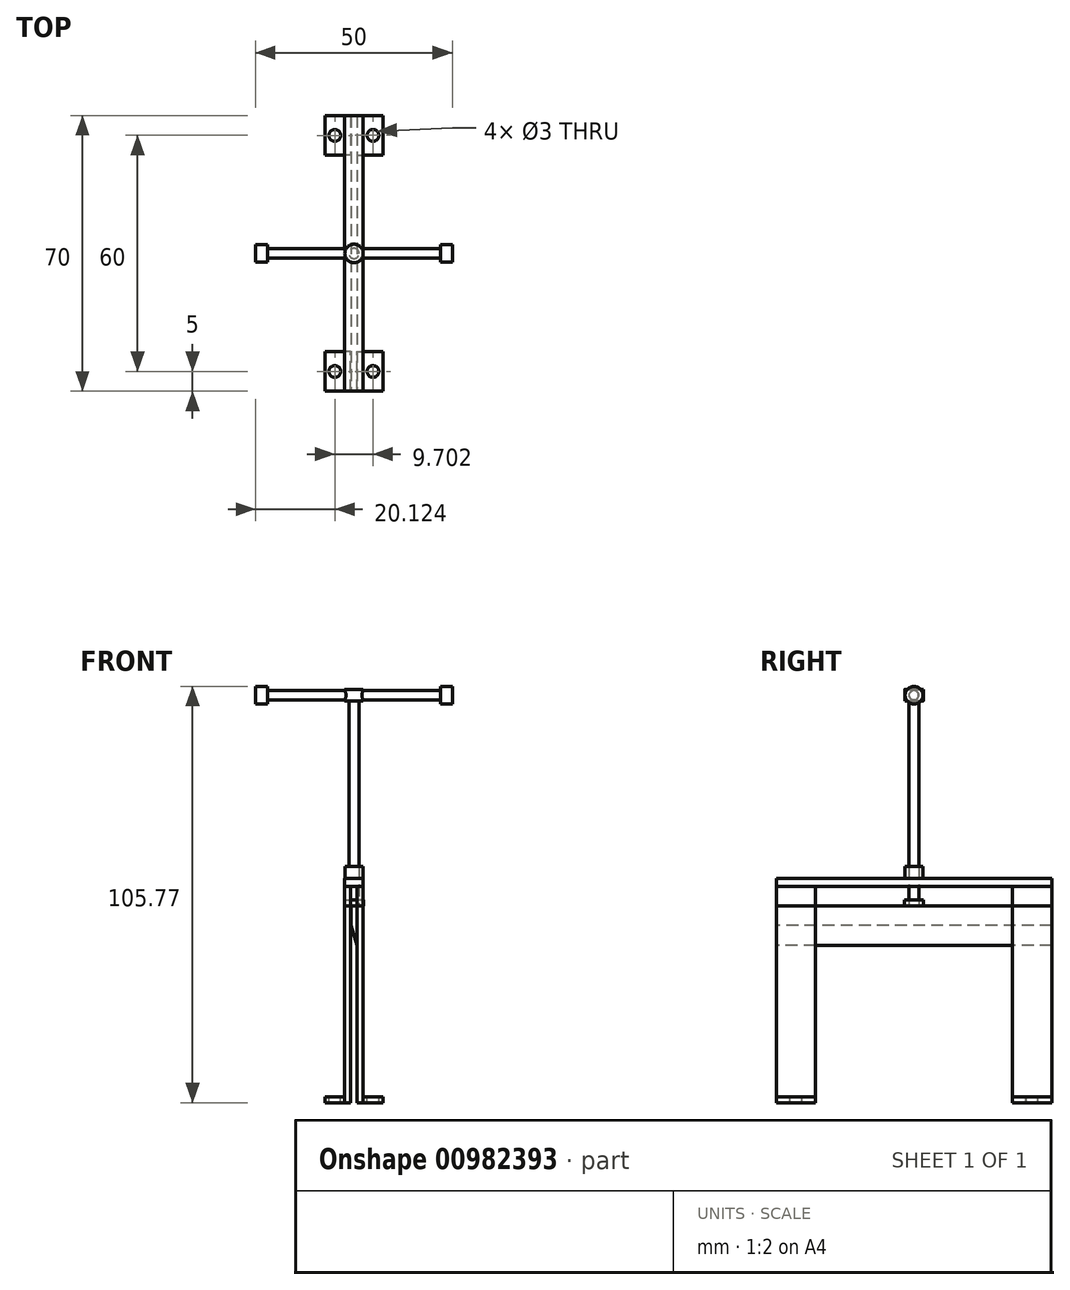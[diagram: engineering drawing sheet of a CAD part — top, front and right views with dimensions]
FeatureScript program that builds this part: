
annotation { "Feature Type Name" : "Feature", "Feature Type Description" : "" }
export const myFeature = defineFeature(function(context is Context, id is Id, definition is map)
    precondition{}
    {
        {
            var Q0;
            Q0=qCreatedBy(makeId("Top.planeOp"),FACE);
            var sketch = newSketch(context, id + "F0", { "sketchPlane" : qUnion([Q0])});
            skLineSegment(sketch, "E0.bottom", {"start": v(-0.77, 35) * mm, "end": v(0.73, 35) * mm});
            skLineSegment(sketch, "E0.top", {"start": v(-0.77, -35) * mm, "end": v(0.73, -35) * mm});
            skLineSegment(sketch, "E0.left", {"start": v(-0.77, 35) * mm, "end": v(-0.77, -35) * mm});
            skLineSegment(sketch, "E0.right", {"start": v(0.73, 35) * mm, "end": v(0.73, -35) * mm});
            skPoint(sketch, "E1.startSnap0", {"position": v(-0.02, 35) * mm});
            skSolve(sketch);
        }
        {
            var Q0;
            Q0 = qSketchRegion(id + "F0", true);
            extrude(context, id + "F1", {"entities" : qUnion([Q0]), "oppositeDirection" : true, "depth" : 10 * mm, "offsetDistance" : 25 * mm});
        }
        {
            var Q0;
            Q0=makeQuery(id+"F1.opExtrude","SWEPT_FACE",FACE,{"disambiguationData":[OSD([sQuery(id+"F0.wireOp",EDGE,"E0.top")])]});
            var sketch = newSketch(context, id + "F2", { "sketchPlane" : qUnion([Q0])});
            skLineSegment(sketch, "E2", {"start": v(-0.77, -5) * mm, "end": v(-0.77, -10) * mm});
            skLineSegment(sketch, "E3", {"start": v(-0.77, -10) * mm, "end": v(0.73, -10) * mm});
            skLineSegment(sketch, "E4", {"start": v(-0.77, -5) * mm, "end": v(0.73, -10) * mm});
            skSolve(sketch);
        }
        {
            var Q0;
            Q0 = qSketchRegion(id + "F2", true);
            extrude(context, id + "F3", {"entities" : qUnion([Q0]), "operationType" : NewBodyOperationType.REMOVE, "endBound" : BoundingType.THROUGH_ALL, "oppositeDirection" : true, "depth" : 25 * mm, "offsetDistance" : 25 * mm});
        }
        {
            var Q0;
            Q0=makeQuery(id+"F1.opExtrude","CAP_FACE",FACE,{"disambiguationData":[OSD([sQuery(id+"F0.wireOp",EDGE,"E0.bottom"),sQuery(id+"F0.wireOp",EDGE,"E0.top"),sQuery(id+"F0.wireOp",EDGE,"E0.left"),sQuery(id+"F0.wireOp",EDGE,"E0.right")])],"isStart":true});
            var sketch = newSketch(context, id + "F4", { "sketchPlane" : qUnion([Q0])});
            skLineSegment(sketch, "E5", {"start": v(-0.77, 35) * mm, "end": v(-0.87, 35) * mm, "construction": true});
            skLineSegment(sketch, "E6", {"start": v(0.73, 35) * mm, "end": v(0.83, 35) * mm, "construction": true});
            skLineSegment(sketch, "E7.bottom", {"start": v(-0.87, 35) * mm, "end": v(-2.37, 35) * mm});
            skLineSegment(sketch, "E7.top", {"start": v(-0.87, 25) * mm, "end": v(-2.37, 25) * mm});
            skLineSegment(sketch, "E7.left", {"start": v(-0.87, 35) * mm, "end": v(-0.87, 25) * mm});
            skLineSegment(sketch, "E7.right", {"start": v(-2.37, 35) * mm, "end": v(-2.37, 25) * mm});
            skLineSegment(sketch, "E8.bottom", {"start": v(0.83, 35) * mm, "end": v(2.33, 35) * mm});
            skLineSegment(sketch, "E8.top", {"start": v(0.83, 25) * mm, "end": v(2.33, 25) * mm});
            skLineSegment(sketch, "E8.left", {"start": v(0.83, 35) * mm, "end": v(0.83, 25) * mm});
            skLineSegment(sketch, "E8.right", {"start": v(2.33, 35) * mm, "end": v(2.33, 25) * mm});
            skLineSegment(sketch, "E9", {"start": v(-0.77, -35) * mm, "end": v(-0.87, -35) * mm, "construction": true});
            skLineSegment(sketch, "E10", {"start": v(0.73, -35) * mm, "end": v(0.83, -35) * mm});
            skLineSegment(sketch, "E11.bottom", {"start": v(0.83, -35) * mm, "end": v(2.33, -35) * mm});
            skLineSegment(sketch, "E11.top", {"start": v(0.83, -25) * mm, "end": v(2.33, -25) * mm});
            skLineSegment(sketch, "E11.left", {"start": v(0.83, -35) * mm, "end": v(0.83, -25) * mm});
            skLineSegment(sketch, "E11.right", {"start": v(2.33, -35) * mm, "end": v(2.33, -25) * mm});
            skLineSegment(sketch, "E12.bottom", {"start": v(-0.87, -35) * mm, "end": v(-2.37, -35) * mm});
            skLineSegment(sketch, "E12.top", {"start": v(-0.87, -25) * mm, "end": v(-2.37, -25) * mm});
            skLineSegment(sketch, "E12.left", {"start": v(-0.87, -35) * mm, "end": v(-0.87, -25) * mm});
            skLineSegment(sketch, "E12.right", {"start": v(-2.37, -35) * mm, "end": v(-2.37, -25) * mm});
            skSolve(sketch);
        }
        {
            var Q0;
            Q0=makeQuery(id+"F4.imprint","IMPRINT",FACE,{"disambiguationData":[TD([[makeQuery(id+"F4.imprint","IMPRINT",EDGE,{"derivedFrom":sQuery(id+"F4.wireOp",EDGE,"E8.bottom")}),-1.0]])]});
            var Q1;
            Q1=makeQuery(id+"F4.imprint","IMPRINT",FACE,{"disambiguationData":[TD([[makeQuery(id+"F4.imprint","IMPRINT",EDGE,{"derivedFrom":sQuery(id+"F4.wireOp",EDGE,"E7.bottom")}),1.0]])]});
            var Q2;
            Q2=makeQuery(id+"F4.imprint","IMPRINT",FACE,{"disambiguationData":[TD([[makeQuery(id+"F4.imprint","IMPRINT",EDGE,{"derivedFrom":sQuery(id+"F4.wireOp",EDGE,"E12.bottom")}),-1.0]])]});
            var Q3;
            Q3=makeQuery(id+"F4.imprint","IMPRINT",FACE,{"disambiguationData":[TD([[makeQuery(id+"F4.imprint","IMPRINT",EDGE,{"derivedFrom":sQuery(id+"F4.wireOp",EDGE,"E11.bottom")}),1.0]])]});
            extrude(context, id + "F5", {"entities" : qUnion([Q0, Q1, Q2, Q3]), "oppositeDirection" : true, "depth" : 50 * mm, "offsetDistance" : 25 * mm});
        }
        {
            var Q0;
            Q0=makeQuery(id+"F4.imprint","IMPRINT",FACE,{"disambiguationData":[TD([[makeQuery(id+"F4.imprint","IMPRINT",EDGE,{"derivedFrom":sQuery(id+"F4.wireOp",EDGE,"E7.bottom")}),1.0]])]});
            var Q1;
            Q1=makeQuery(id+"F4.imprint","IMPRINT",FACE,{"disambiguationData":[TD([[makeQuery(id+"F4.imprint","IMPRINT",EDGE,{"derivedFrom":sQuery(id+"F4.wireOp",EDGE,"E8.bottom")}),-1.0]])]});
            var Q2;
            Q2=makeQuery(id+"F4.imprint","IMPRINT",FACE,{"disambiguationData":[TD([[makeQuery(id+"F4.imprint","IMPRINT",EDGE,{"derivedFrom":sQuery(id+"F4.wireOp",EDGE,"E12.bottom")}),-1.0]])]});
            var Q3;
            Q3=makeQuery(id+"F4.imprint","IMPRINT",FACE,{"disambiguationData":[TD([[makeQuery(id+"F4.imprint","IMPRINT",EDGE,{"derivedFrom":sQuery(id+"F4.wireOp",EDGE,"E11.bottom")}),1.0]])]});
            extrude(context, id + "F6", {"entities" : qUnion([Q0, Q1, Q2, Q3]), "depth" : 5 * mm, "offsetDistance" : 25 * mm});
        }
        {
            var Q0;
            Q0=makeQuery(id+"F6.opExtrude","CAP_FACE",FACE,{"disambiguationData":[OSD([sQuery(id+"F4.wireOp",EDGE,"E7.bottom"),sQuery(id+"F4.wireOp",EDGE,"E7.top"),sQuery(id+"F4.wireOp",EDGE,"E7.left"),sQuery(id+"F4.wireOp",EDGE,"E7.right")])],"isStart":false});
            var sketch = newSketch(context, id + "F7", { "sketchPlane" : qUnion([Q0])});
            skLineSegment(sketch, "E13.bottom", {"start": v(-2.37, 35) * mm, "end": v(2.33, 35) * mm});
            skLineSegment(sketch, "E13.top", {"start": v(-2.37, -35) * mm, "end": v(2.33, -35) * mm});
            skLineSegment(sketch, "E13.left", {"start": v(-2.37, 35) * mm, "end": v(-2.37, -35) * mm});
            skLineSegment(sketch, "E13.right", {"start": v(2.33, 35) * mm, "end": v(2.33, -35) * mm});
            skSolve(sketch);
        }
        {
            var Q0;
            Q0 = qSketchRegion(id + "F7", true);
            extrude(context, id + "F8", {"entities" : qUnion([Q0]), "depth" : 2 * mm, "offsetDistance" : 25 * mm});
        }
        {
            var Q0;
            Q0=makeQuery(id+"F8.opExtrude","CAP_FACE",FACE,{"disambiguationData":[OSD([sQuery(id+"F7.wireOp",EDGE,"E13.bottom"),sQuery(id+"F7.wireOp",EDGE,"E13.top"),sQuery(id+"F7.wireOp",EDGE,"E13.left"),sQuery(id+"F7.wireOp",EDGE,"E13.right")])],"isStart":false});
            var sketch = newSketch(context, id + "F9", { "sketchPlane" : qUnion([Q0])});
            skCircle(sketch, "E14", {"center": v(0, 0) * mm, "radius": 2.31 * mm});
            skSolve(sketch);
        }
        {
            var Q0;
            Q0=makeQuery(id+"F4.imprint","IMPRINT",FACE,{"disambiguationData":[TD([[makeQuery(id+"F4.imprint","IMPRINT",EDGE,{"derivedFrom":makeQuery(id+"F1.opExtrude","CAP_EDGE",EDGE,{"disambiguationData":[OSD([sQuery(id+"F0.wireOp",EDGE,"E0.bottom")])],"isStart":true})}),-1.0]])]});
            var sketch = newSketch(context, id + "F10", { "sketchPlane" : qUnion([Q0])});
            skCircle(sketch, "E15", {"center": v(0, 0) * mm, "radius": 1.3 * mm});
            skSolve(sketch);
        }
        {
            var Q0;
            {var subQ0=sQuery(id+"F10.wireOp",EDGE,"E15");var subQ1=makeQuery(id+"F4.imprint","IMPRINT",EDGE,{"derivedFrom":makeQuery(id+"F1.opExtrude","CAP_EDGE",EDGE,{"disambiguationData":[OSD([sQuery(id+"F0.wireOp",EDGE,"E0.left")])],"isStart":true})});var subQ2=makeQuery(id+"F10.imprint","INTERSECT",VERTEX,{"disambiguationData":[OD(0.0)],"derivedFrom":[subQ1,subQ0]});Q0=makeQuery(id+"F10.imprint","IMPRINT",FACE,{"disambiguationData":[TD([[makeQuery(id+"F10.imprint","IMPRINT",EDGE,{"disambiguationData":[TD([[subQ2,-1.0]])],"derivedFrom":subQ0}),1.0]])]});}
            var Q1;
            {var subQ0=sQuery(id+"F10.wireOp",EDGE,"E15");var subQ1=makeQuery(id+"F4.imprint","IMPRINT",EDGE,{"derivedFrom":makeQuery(id+"F1.opExtrude","CAP_EDGE",EDGE,{"disambiguationData":[OSD([sQuery(id+"F0.wireOp",EDGE,"E0.right")])],"isStart":true})});var subQ2=makeQuery(id+"F10.imprint","INTERSECT",VERTEX,{"disambiguationData":[OD(0.0)],"derivedFrom":[subQ1,subQ0]});Q1=makeQuery(id+"F10.imprint","IMPRINT",FACE,{"disambiguationData":[TD([[makeQuery(id+"F10.imprint","IMPRINT",EDGE,{"disambiguationData":[TD([[subQ2,1.0]])],"derivedFrom":subQ0}),1.0]])]});}
            var Q2;
            {var subQ0=sQuery(id+"F10.wireOp",EDGE,"E15");var subQ1=makeQuery(id+"F4.imprint","IMPRINT",EDGE,{"derivedFrom":makeQuery(id+"F1.opExtrude","CAP_EDGE",EDGE,{"disambiguationData":[OSD([sQuery(id+"F0.wireOp",EDGE,"E0.left")])],"isStart":true})});var subQ2=makeQuery(id+"F10.imprint","INTERSECT",VERTEX,{"disambiguationData":[OD(0.0)],"derivedFrom":[subQ1,subQ0]});Q2=makeQuery(id+"F10.imprint","IMPRINT",FACE,{"disambiguationData":[TD([[makeQuery(id+"F10.imprint","IMPRINT",EDGE,{"disambiguationData":[TD([[subQ2,1.0]])],"derivedFrom":subQ0}),1.0]])]});}
            extrude(context, id + "F11", {"entities" : qUnion([Q0, Q1, Q2]), "depth" : 55 * mm, "offsetDistance" : 25 * mm});
        }
        {
            var Q0;
            Q0=makeQuery(id+"F9.imprint","IMPRINT",FACE,{"disambiguationData":[TD([[makeQuery(id+"F9.imprint","IMPRINT",EDGE,{"derivedFrom":sQuery(id+"F9.wireOp",EDGE,"E14")}),1.0]])]});
            extrude(context, id + "F12", {"entities" : qUnion([Q0]), "depth" : 3 * mm, "offsetDistance" : 25 * mm});
        }
        {
            var Q0;
            Q0=makeQuery(id+"F11.opExtrude","CAP_FACE",FACE,{"disambiguationData":[OSD([sQuery(id+"F10.wireOp",EDGE,"E15")])],"isStart":false});
            var sketch = newSketch(context, id + "F13", { "sketchPlane" : qUnion([Q0])});
            skCircle(sketch, "E16", {"center": v(0, 0) * mm, "radius": 2.35 * mm});
            skSolve(sketch);
        }
        {
            var Q0;
            Q0=makeQuery(id+"F13.imprint","IMPRINT",FACE,{"disambiguationData":[TD([[makeQuery(id+"F13.imprint","IMPRINT",EDGE,{"derivedFrom":sQuery(id+"F13.wireOp",EDGE,"E16")}),1.0]])]});
            extrude(context, id + "F14", {"entities" : qUnion([Q0]), "operationType" : NewBodyOperationType.ADD, "oppositeDirection" : true, "depth" : 3 * mm, "offsetDistance" : 25 * mm});
        }
        {
            var Q0;
            Q0=qCreatedBy(makeId("Right.planeOp"),FACE);
            var sketch = newSketch(context, id + "F15", { "sketchPlane" : qUnion([Q0])});
            skLineSegment(sketch, "E17", {"start": v(0, 55.02) * mm, "end": v(0, 52) * mm, "construction": true});
            skLineSegment(sketch, "E18", {"start": v(0, 53.51) * mm, "end": v(-2.35, 53.51) * mm, "construction": true});
            skCircle(sketch, "E19", {"center": v(0, 53.51) * mm, "radius": 1.19 * mm});
            skSolve(sketch);
        }
        {
            var Q0;
            Q0 = qSketchRegion(id + "F15", true);
            extrude(context, id + "F16", {"entities" : qUnion([Q0]), "operationType" : NewBodyOperationType.ADD, "oppositeDirection" : true, "depth" : 25 * mm, "offsetDistance" : 25 * mm});
        }
        {
            var Q0;
            Q0=makeQuery(id+"F16.opExtrude","CAP_FACE",FACE,{"disambiguationData":[OSD([sQuery(id+"F15.wireOp",EDGE,"E19")])],"isStart":false});
            var sketch = newSketch(context, id + "F17", { "sketchPlane" : qUnion([Q0])});
            skCircle(sketch, "E20", {"center": v(0, 53.51) * mm, "radius": 2.25 * mm});
            skSolve(sketch);
        }
        {
            var Q0;
            Q0=makeQuery(id+"F17.imprint","IMPRINT",FACE,{"disambiguationData":[TD([[makeQuery(id+"F17.imprint","IMPRINT",EDGE,{"derivedFrom":sQuery(id+"F17.wireOp",EDGE,"E20")}),1.0]])]});
            extrude(context, id + "F18", {"entities" : qUnion([Q0]), "operationType" : NewBodyOperationType.ADD, "oppositeDirection" : true, "depth" : 3 * mm, "offsetDistance" : 25 * mm});
        }
        {
            var Q0;
            Q0 = qSketchRegion(id + "F15", true);
            extrude(context, id + "F19", {"entities" : qUnion([Q0]), "operationType" : NewBodyOperationType.ADD, "depth" : 25 * mm, "offsetDistance" : 25 * mm});
        }
        {
            var Q0;
            Q0=makeQuery(id+"F19.opExtrude","CAP_FACE",FACE,{"disambiguationData":[OSD([sQuery(id+"F15.wireOp",EDGE,"E19")])],"isStart":false});
            var sketch = newSketch(context, id + "F20", { "sketchPlane" : qUnion([Q0])});
            skCircle(sketch, "E21", {"center": v(0, 53.51) * mm, "radius": 2.26 * mm});
            skSolve(sketch);
        }
        {
            var Q0;
            Q0=makeQuery(id+"F20.imprint","IMPRINT",FACE,{"disambiguationData":[TD([[makeQuery(id+"F20.imprint","IMPRINT",EDGE,{"derivedFrom":sQuery(id+"F20.wireOp",EDGE,"E21")}),1.0]])]});
            extrude(context, id + "F21", {"entities" : qUnion([Q0]), "operationType" : NewBodyOperationType.ADD, "oppositeDirection" : true, "depth" : 3 * mm, "offsetDistance" : 25 * mm});
        }
        {
            var Q0;
            Q0=makeQuery(id+"F5.opExtrude","CAP_FACE",FACE,{"disambiguationData":[OSD([sQuery(id+"F4.wireOp",EDGE,"E12.bottom"),sQuery(id+"F4.wireOp",EDGE,"E12.top"),sQuery(id+"F4.wireOp",EDGE,"E12.left"),sQuery(id+"F4.wireOp",EDGE,"E12.right")])],"isStart":false});
            var sketch = newSketch(context, id + "F22", { "sketchPlane" : qUnion([Q0])});
            skLineSegment(sketch, "E22.bottom", {"start": v(-2.37, 25) * mm, "end": v(-7.37, 25) * mm});
            skLineSegment(sketch, "E22.top", {"start": v(-2.37, 35) * mm, "end": v(-7.37, 35) * mm});
            skLineSegment(sketch, "E22.left", {"start": v(-2.37, 25) * mm, "end": v(-2.37, 35) * mm});
            skLineSegment(sketch, "E22.right", {"start": v(-7.37, 25) * mm, "end": v(-7.37, 35) * mm});
            skLineSegment(sketch, "E23.bottom", {"start": v(2.33, 35) * mm, "end": v(7.33, 35) * mm});
            skLineSegment(sketch, "E23.top", {"start": v(2.33, 25) * mm, "end": v(7.33, 25) * mm});
            skLineSegment(sketch, "E23.left", {"start": v(2.33, 35) * mm, "end": v(2.33, 25) * mm});
            skLineSegment(sketch, "E23.right", {"start": v(7.33, 35) * mm, "end": v(7.33, 25) * mm});
            skSolve(sketch);
        }
        {
            var Q0;
            Q0=makeQuery(id+"F22.imprint","IMPRINT",FACE,{"disambiguationData":[TD([[makeQuery(id+"F22.imprint","IMPRINT",EDGE,{"derivedFrom":sQuery(id+"F22.wireOp",EDGE,"E23.bottom")}),-1.0]])]});
            var Q1;
            Q1=makeQuery(id+"F22.imprint","IMPRINT",FACE,{"disambiguationData":[TD([[makeQuery(id+"F22.imprint","IMPRINT",EDGE,{"derivedFrom":sQuery(id+"F22.wireOp",EDGE,"E22.bottom")}),-1.0]])]});
            extrude(context, id + "F23", {"entities" : qUnion([Q0, Q1]), "oppositeDirection" : true, "depth" : 1.5 * mm, "offsetDistance" : 25 * mm});
        }
        {
            var Q0;
            Q0=makeQuery(id+"F5.opExtrude","CAP_FACE",FACE,{"disambiguationData":[OSD([sQuery(id+"F4.wireOp",EDGE,"E8.bottom"),sQuery(id+"F4.wireOp",EDGE,"E8.top"),sQuery(id+"F4.wireOp",EDGE,"E8.left"),sQuery(id+"F4.wireOp",EDGE,"E8.right")])],"isStart":false});
            var sketch = newSketch(context, id + "F24", { "sketchPlane" : qUnion([Q0])});
            skLineSegment(sketch, "E24.bottom", {"start": v(-2.38, -24.99) * mm, "end": v(-7.37, -24.99) * mm});
            skLineSegment(sketch, "E24.top", {"start": v(-2.38, -34.99) * mm, "end": v(-7.37, -34.99) * mm});
            skLineSegment(sketch, "E24.left", {"start": v(-2.38, -24.99) * mm, "end": v(-2.38, -34.99) * mm});
            skLineSegment(sketch, "E24.right", {"start": v(-7.37, -24.99) * mm, "end": v(-7.37, -34.99) * mm});
            skLineSegment(sketch, "E25.bottom", {"start": v(2.33, -25) * mm, "end": v(7.33, -25) * mm});
            skLineSegment(sketch, "E25.top", {"start": v(2.33, -35) * mm, "end": v(7.33, -35) * mm});
            skLineSegment(sketch, "E25.left", {"start": v(2.33, -25) * mm, "end": v(2.33, -35) * mm});
            skLineSegment(sketch, "E25.right", {"start": v(7.33, -25) * mm, "end": v(7.33, -35) * mm});
            skSolve(sketch);
        }
        {
            var Q0;
            Q0=makeQuery(id+"F24.imprint","IMPRINT",FACE,{"disambiguationData":[TD([[makeQuery(id+"F24.imprint","IMPRINT",EDGE,{"derivedFrom":sQuery(id+"F24.wireOp",EDGE,"E25.bottom")}),-1.0]])]});
            var Q1;
            Q1=makeQuery(id+"F24.imprint","IMPRINT",FACE,{"disambiguationData":[TD([[makeQuery(id+"F24.imprint","IMPRINT",EDGE,{"derivedFrom":sQuery(id+"F24.wireOp",EDGE,"E24.bottom")}),1.0]])]});
            extrude(context, id + "F25", {"entities" : qUnion([Q0, Q1]), "operationType" : NewBodyOperationType.ADD, "oppositeDirection" : true, "depth" : 1.5 * mm, "offsetDistance" : 25 * mm});
        }
        {
            var Q0;
            Q0=makeQuery(id+"F25.opExtrude","CAP_FACE",FACE,{"disambiguationData":[OSD([sQuery(id+"F24.wireOp",EDGE,"E25.bottom"),sQuery(id+"F24.wireOp",EDGE,"E25.top"),sQuery(id+"F24.wireOp",EDGE,"E25.left"),sQuery(id+"F24.wireOp",EDGE,"E25.right")])],"isStart":false});
            var sketch = newSketch(context, id + "F26", { "sketchPlane" : qUnion([Q0])});
            skLineSegment(sketch, "E26", {"start": v(4.83, 35) * mm, "end": v(4.83, 25) * mm, "construction": true});
            skCircle(sketch, "E27", {"center": v(4.83, 30) * mm, "radius": 1.5 * mm});
            skSolve(sketch);
        }
        {
            var Q0;
            Q0=makeQuery(id+"F25.opExtrude","CAP_FACE",FACE,{"disambiguationData":[OSD([sQuery(id+"F24.wireOp",EDGE,"E24.bottom"),sQuery(id+"F24.wireOp",EDGE,"E24.top"),sQuery(id+"F24.wireOp",EDGE,"E24.left"),sQuery(id+"F24.wireOp",EDGE,"E24.right")])],"isStart":false});
            var sketch = newSketch(context, id + "F27", { "sketchPlane" : qUnion([Q0])});
            skLineSegment(sketch, "E28", {"start": v(-4.88, 34.99) * mm, "end": v(-4.88, 24.99) * mm, "construction": true});
            skCircle(sketch, "E29", {"center": v(-4.88, 29.99) * mm, "radius": 1.5 * mm});
            skSolve(sketch);
        }
        {
            var Q0;
            Q0=makeQuery(id+"F27.imprint","IMPRINT",FACE,{"disambiguationData":[TD([[makeQuery(id+"F27.imprint","IMPRINT",EDGE,{"derivedFrom":sQuery(id+"F27.wireOp",EDGE,"E29")}),1.0]])]});
            var Q1;
            Q1=sQuery(id+"F27.wireOp",EDGE,"E29");
            extrude(context, id + "F28", {"entities" : qUnion([Q0]), "operationType" : NewBodyOperationType.REMOVE, "surfaceEntities" : qUnion([Q1]), "endBound" : BoundingType.THROUGH_ALL, "oppositeDirection" : true, "depth" : 25 * mm, "offsetDistance" : 25 * mm});
        }
        {
            var Q0;
            Q0=makeQuery(id+"F26.imprint","IMPRINT",FACE,{"disambiguationData":[TD([[makeQuery(id+"F26.imprint","IMPRINT",EDGE,{"derivedFrom":sQuery(id+"F26.wireOp",EDGE,"E27")}),1.0]])]});
            var Q1;
            Q1=sQuery(id+"F26.wireOp",EDGE,"E27");
            extrude(context, id + "F29", {"entities" : qUnion([Q0]), "operationType" : NewBodyOperationType.REMOVE, "surfaceEntities" : qUnion([Q1]), "endBound" : BoundingType.THROUGH_ALL, "oppositeDirection" : true, "depth" : 25 * mm, "offsetDistance" : 25 * mm});
        }
        {
            var Q0;
            Q0=makeQuery(id+"F23.opExtrude","CAP_FACE",FACE,{"disambiguationData":[OSD([sQuery(id+"F22.wireOp",EDGE,"E23.bottom"),sQuery(id+"F22.wireOp",EDGE,"E23.top"),sQuery(id+"F22.wireOp",EDGE,"E23.left"),sQuery(id+"F22.wireOp",EDGE,"E23.right")])],"isStart":false});
            var sketch = newSketch(context, id + "F30", { "sketchPlane" : qUnion([Q0])});
            skLineSegment(sketch, "E30", {"start": v(4.83, -25) * mm, "end": v(4.83, -35) * mm, "construction": true});
            skCircle(sketch, "E31", {"center": v(4.83, -30) * mm, "radius": 1.5 * mm});
            skSolve(sketch);
        }
        {
            var Q0;
            Q0=makeQuery(id+"F23.opExtrude","CAP_FACE",FACE,{"disambiguationData":[OSD([sQuery(id+"F22.wireOp",EDGE,"E22.bottom"),sQuery(id+"F22.wireOp",EDGE,"E22.top"),sQuery(id+"F22.wireOp",EDGE,"E22.left"),sQuery(id+"F22.wireOp",EDGE,"E22.right")])],"isStart":false});
            var sketch = newSketch(context, id + "F31", { "sketchPlane" : qUnion([Q0])});
            skLineSegment(sketch, "E32", {"start": v(-4.87, -25) * mm, "end": v(-4.87, -35) * mm, "construction": true});
            skCircle(sketch, "E33", {"center": v(-4.87, -30) * mm, "radius": 1.5 * mm});
            skSolve(sketch);
        }
        {
            var Q0;
            Q0=makeQuery(id+"F31.imprint","IMPRINT",FACE,{"disambiguationData":[TD([[makeQuery(id+"F31.imprint","IMPRINT",EDGE,{"derivedFrom":sQuery(id+"F31.wireOp",EDGE,"E33")}),1.0]])]});
            var Q1;
            Q1=sQuery(id+"F31.wireOp",EDGE,"E33");
            extrude(context, id + "F32", {"entities" : qUnion([Q0]), "operationType" : NewBodyOperationType.REMOVE, "surfaceEntities" : qUnion([Q1]), "endBound" : BoundingType.THROUGH_ALL, "oppositeDirection" : true, "depth" : 25 * mm, "offsetDistance" : 25 * mm});
        }
        {
            var Q0;
            Q0=makeQuery(id+"F30.imprint","IMPRINT",FACE,{"disambiguationData":[TD([[makeQuery(id+"F30.imprint","IMPRINT",EDGE,{"derivedFrom":sQuery(id+"F30.wireOp",EDGE,"E31")}),1.0]])]});
            var Q1;
            Q1=sQuery(id+"F30.wireOp",EDGE,"E31");
            extrude(context, id + "F33", {"entities" : qUnion([Q0]), "operationType" : NewBodyOperationType.REMOVE, "surfaceEntities" : qUnion([Q1]), "endBound" : BoundingType.THROUGH_ALL, "oppositeDirection" : true, "depth" : 25 * mm, "offsetDistance" : 25 * mm});
        }
        {
            var Q0;
            Q0=makeQuery(id+"F4.imprint","IMPRINT",FACE,{"disambiguationData":[TD([[makeQuery(id+"F4.imprint","IMPRINT",EDGE,{"derivedFrom":makeQuery(id+"F1.opExtrude","CAP_EDGE",EDGE,{"disambiguationData":[OSD([sQuery(id+"F0.wireOp",EDGE,"E0.bottom")])],"isStart":true})}),-1.0]])]});
            var sketch = newSketch(context, id + "F34", { "sketchPlane" : qUnion([Q0])});
            skCircle(sketch, "E34", {"center": v(0, 0) * mm, "radius": 2.38 * mm});
            skSolve(sketch);
        }
        {
            var Q0;
            {var subQ0=sQuery(id+"F34.wireOp",EDGE,"E34");var subQ1=makeQuery(id+"F4.imprint","IMPRINT",EDGE,{"derivedFrom":makeQuery(id+"F1.opExtrude","CAP_EDGE",EDGE,{"disambiguationData":[OSD([sQuery(id+"F0.wireOp",EDGE,"E0.left")])],"isStart":true})});var subQ2=makeQuery(id+"F34.imprint","INTERSECT",VERTEX,{"disambiguationData":[OD(0.0)],"derivedFrom":[subQ1,subQ0]});Q0=makeQuery(id+"F34.imprint","IMPRINT",FACE,{"disambiguationData":[TD([[makeQuery(id+"F34.imprint","IMPRINT",EDGE,{"disambiguationData":[TD([[subQ2,-1.0]])],"derivedFrom":subQ0}),1.0]])]});}
            var Q1;
            {var subQ0=sQuery(id+"F34.wireOp",EDGE,"E34");var subQ1=makeQuery(id+"F4.imprint","IMPRINT",EDGE,{"derivedFrom":makeQuery(id+"F1.opExtrude","CAP_EDGE",EDGE,{"disambiguationData":[OSD([sQuery(id+"F0.wireOp",EDGE,"E0.left")])],"isStart":true})});var subQ2=makeQuery(id+"F34.imprint","INTERSECT",VERTEX,{"disambiguationData":[OD(0.0)],"derivedFrom":[subQ1,subQ0]});Q1=makeQuery(id+"F34.imprint","IMPRINT",FACE,{"disambiguationData":[TD([[makeQuery(id+"F34.imprint","IMPRINT",EDGE,{"disambiguationData":[TD([[subQ2,1.0]])],"derivedFrom":subQ0}),1.0]])]});}
            var Q2;
            {var subQ0=sQuery(id+"F34.wireOp",EDGE,"E34");var subQ1=makeQuery(id+"F4.imprint","IMPRINT",EDGE,{"derivedFrom":makeQuery(id+"F1.opExtrude","CAP_EDGE",EDGE,{"disambiguationData":[OSD([sQuery(id+"F0.wireOp",EDGE,"E0.right")])],"isStart":true})});var subQ2=makeQuery(id+"F34.imprint","INTERSECT",VERTEX,{"disambiguationData":[OD(0.0)],"derivedFrom":[subQ1,subQ0]});Q2=makeQuery(id+"F34.imprint","IMPRINT",FACE,{"disambiguationData":[TD([[makeQuery(id+"F34.imprint","IMPRINT",EDGE,{"disambiguationData":[TD([[subQ2,1.0]])],"derivedFrom":subQ0}),1.0]])]});}
            extrude(context, id + "F35", {"entities" : qUnion([Q0, Q1, Q2]), "depth" : 1.5 * mm, "offsetDistance" : 25 * mm});
        }
        {
            var Q0;
            Q0=makeQuery(id+"F11.opExtrude","CAP_FACE",FACE,{"disambiguationData":[OSD([sQuery(id+"F10.wireOp",EDGE,"E15")])],"isStart":true});
            var sketch = newSketch(context, id + "F36", { "sketchPlane" : qUnion([Q0])});
            skCircle(sketch, "E35", {"center": v(0, 0) * mm, "radius": 1.77 * mm});
            skSolve(sketch);
        }
        {
            var Q0;
            Q0=sQuery(id+"F36.wireOp",EDGE,"E35");
            extrude(context, id + "F37", {"bodyType" : ToolBodyType.SURFACE, "surfaceEntities" : qUnion([Q0]), "oppositeDirection" : true, "depth" : 1.1 * mm, "offsetDistance" : 25 * mm});
        }
    });
